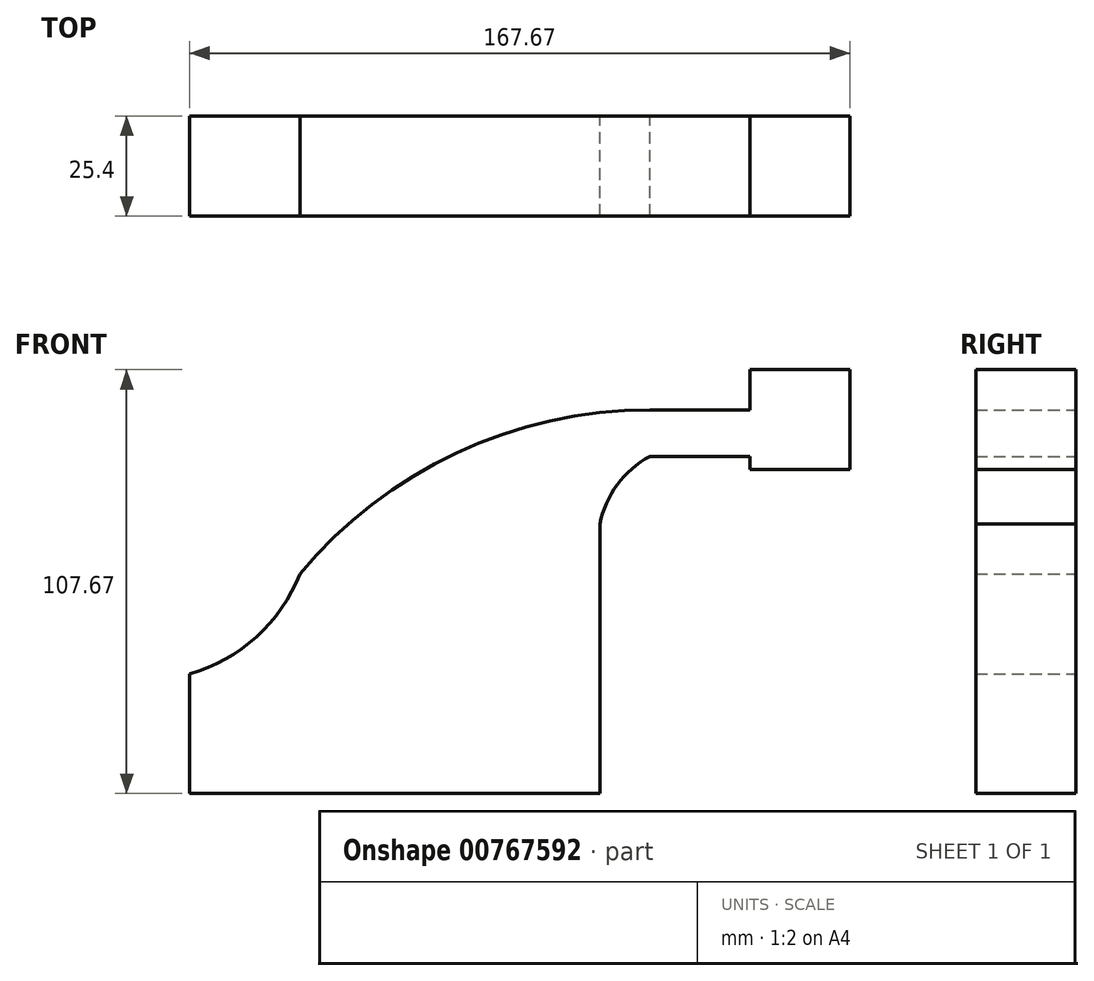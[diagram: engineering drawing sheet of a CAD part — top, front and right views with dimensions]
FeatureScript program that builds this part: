
annotation { "Feature Type Name" : "Feature", "Feature Type Description" : "" }
export const myFeature = defineFeature(function(context is Context, id is Id, definition is map)
    precondition{}
    {
        {
            var Q0;
            Q0=qCreatedBy(makeId("Front.planeOp"),FACE);
            var sketch = newSketch(context, id + "F0", { "sketchPlane" : qUnion([Q0])});
            skLineSegment(sketch, "E0.bottom", {"start": v(0, 0) * mm, "end": v(-76.2, 0) * mm});
            skLineSegment(sketch, "E0.top", {"start": v(0, 25.4) * mm, "end": v(-76.2, 25.4) * mm});
            skLineSegment(sketch, "E0.left", {"start": v(0, 0) * mm, "end": v(0, 25.4) * mm});
            skLineSegment(sketch, "E0.right", {"start": v(-76.2, 0) * mm, "end": v(-76.2, 25.4) * mm});
            skLineSegment(sketch, "E1", {"start": v(0, 25.4) * mm, "end": v(0, 38.1) * mm});
            skArc(sketch, "E2", {"start": v(12.7, 55.33) * mm, "mid": v(4.45, 48.12) * mm, "end": v(0, 38.1) * mm});
            skLineSegment(sketch, "E3", {"start": v(12.7, 55.33) * mm, "end": v(38.1, 55.33) * mm});
            skLineSegment(sketch, "E4.bottom", {"start": v(38.1, 77.34) * mm, "end": v(63.5, 77.34) * mm});
            skLineSegment(sketch, "E4.top", {"start": v(38.1, 51.94) * mm, "end": v(63.5, 51.94) * mm});
            skLineSegment(sketch, "E4.left", {"start": v(38.1, 77.34) * mm, "end": v(38.1, 51.94) * mm});
            skLineSegment(sketch, "E4.right", {"start": v(63.5, 77.34) * mm, "end": v(63.5, 51.94) * mm});
            skLineSegment(sketch, "E5", {"start": v(-11.71, 25.4) * mm, "end": v(-11.71, 38.1) * mm});
            skArc(sketch, "E6", {"start": v(12.7, 67.1) * mm, "mid": v(-3.37, 55.85) * mm, "end": v(-11.71, 38.1) * mm});
            skLineSegment(sketch, "E7", {"start": v(12.7, 67.1) * mm, "end": v(38.1, 67.1) * mm});
            skPoint(sketch, "E7.endSnap0", {"position": v(38.1, 64.64) * mm});
            skArc(sketch, "E8", {"start": v(12.7, 67.1) * mm, "mid": v(-36.4, 56.16) * mm, "end": v(-76.2, 25.4) * mm});
            skLineSegment(sketch, "E9.bottom", {"start": v(0, 0) * mm, "end": v(-104.17, 0) * mm});
            skLineSegment(sketch, "E9.top", {"start": v(0, -30.33) * mm, "end": v(-104.17, -30.33) * mm});
            skLineSegment(sketch, "E9.left", {"start": v(0, 0) * mm, "end": v(0, -30.33) * mm});
            skLineSegment(sketch, "E9.right", {"start": v(-104.17, 0) * mm, "end": v(-104.17, -30.33) * mm});
            skArc(sketch, "E10", {"start": v(-104.17, 0) * mm, "mid": v(-87.23, 9.45) * mm, "end": v(-76.2, 25.4) * mm});
            skSolve(sketch);
        }
        {
            var Q0;
            Q0 = qSketchRegion(id + "F0", true);
            extrude(context, id + "F1", {"entities" : qUnion([Q0]), "depth" : 25.4 * mm, "offsetDistance" : 25.4 * mm});
        }
    });
